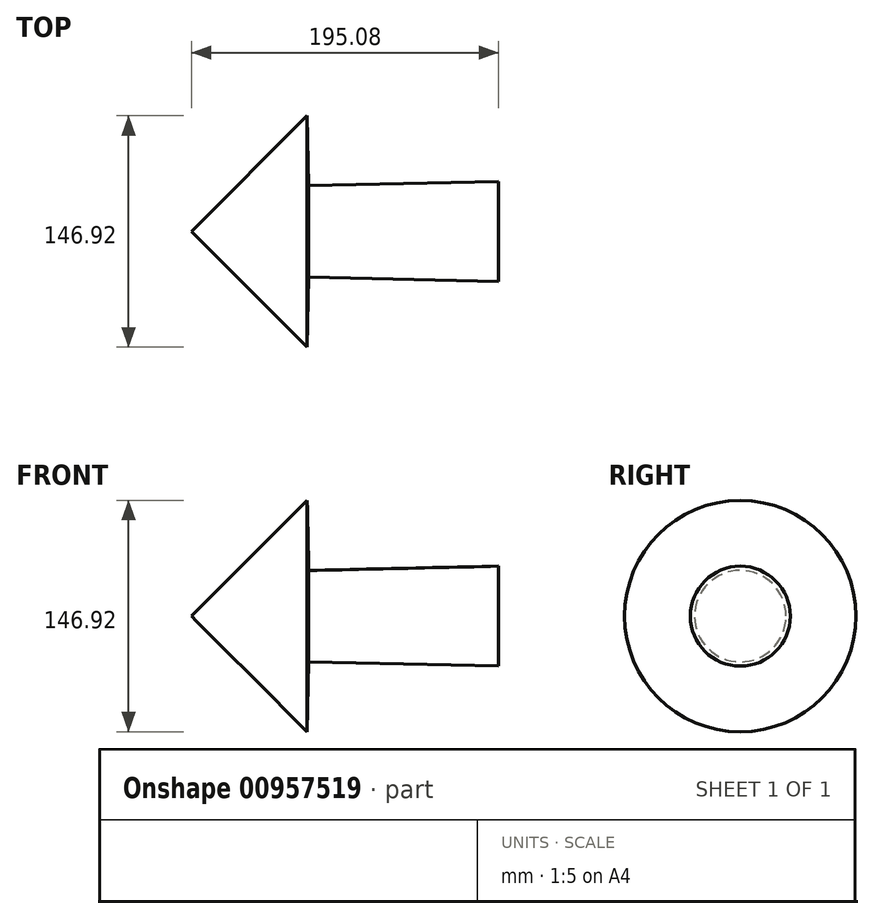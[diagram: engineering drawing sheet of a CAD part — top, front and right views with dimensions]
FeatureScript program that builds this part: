
annotation { "Feature Type Name" : "Feature", "Feature Type Description" : "" }
export const myFeature = defineFeature(function(context is Context, id is Id, definition is map)
    precondition{}
    {
        {
            var Q0;
            Q0=qCreatedBy(makeId("Front.planeOp"),FACE);
            var sketch = newSketch(context, id + "F0", { "sketchPlane" : qUnion([Q0])});
            skLineSegment(sketch, "E0", {"start": v(0, 0) * mm, "end": v(255.44, 0) * mm});
            skLineSegment(sketch, "E1", {"start": v(0, 0) * mm, "end": v(73.46, 73.46) * mm});
            skLineSegment(sketch, "E2", {"start": v(73.46, 73.46) * mm, "end": v(73.46, 73.46) * mm});
            skLineSegment(sketch, "E3", {"start": v(74.46, 29.02) * mm, "end": v(73.46, 73.46) * mm});
            skLineSegment(sketch, "E4", {"start": v(74.46, 29.02) * mm, "end": v(195.08, 31.75) * mm});
            skLineSegment(sketch, "E5", {"start": v(195.08, 31.75) * mm, "end": v(195.08, 0) * mm});
            skSolve(sketch);
        }
        {
            var Q0;
            {var subQ0=sQuery(id+"F0.wireOp",EDGE,"E1");Q0=makeQuery(id+"F0.imprint","IMPRINT",FACE,{"disambiguationData":[TD([[makeQuery(id+"F0.imprint","IMPRINT",EDGE,{"derivedFrom":subQ0}),-1.0]])]});}
            var Q1;
            Q1=sQuery(id+"F0.wireOp",EDGE,"E0");
            revolve(context, id + "F1", {"surfaceOperationType" : NewSurfaceOperationType.NEW, "entities" : qUnion([Q0]), "axis" : qUnion([Q1]), "revolveType" : RevolveType.FULL});
        }
    });
